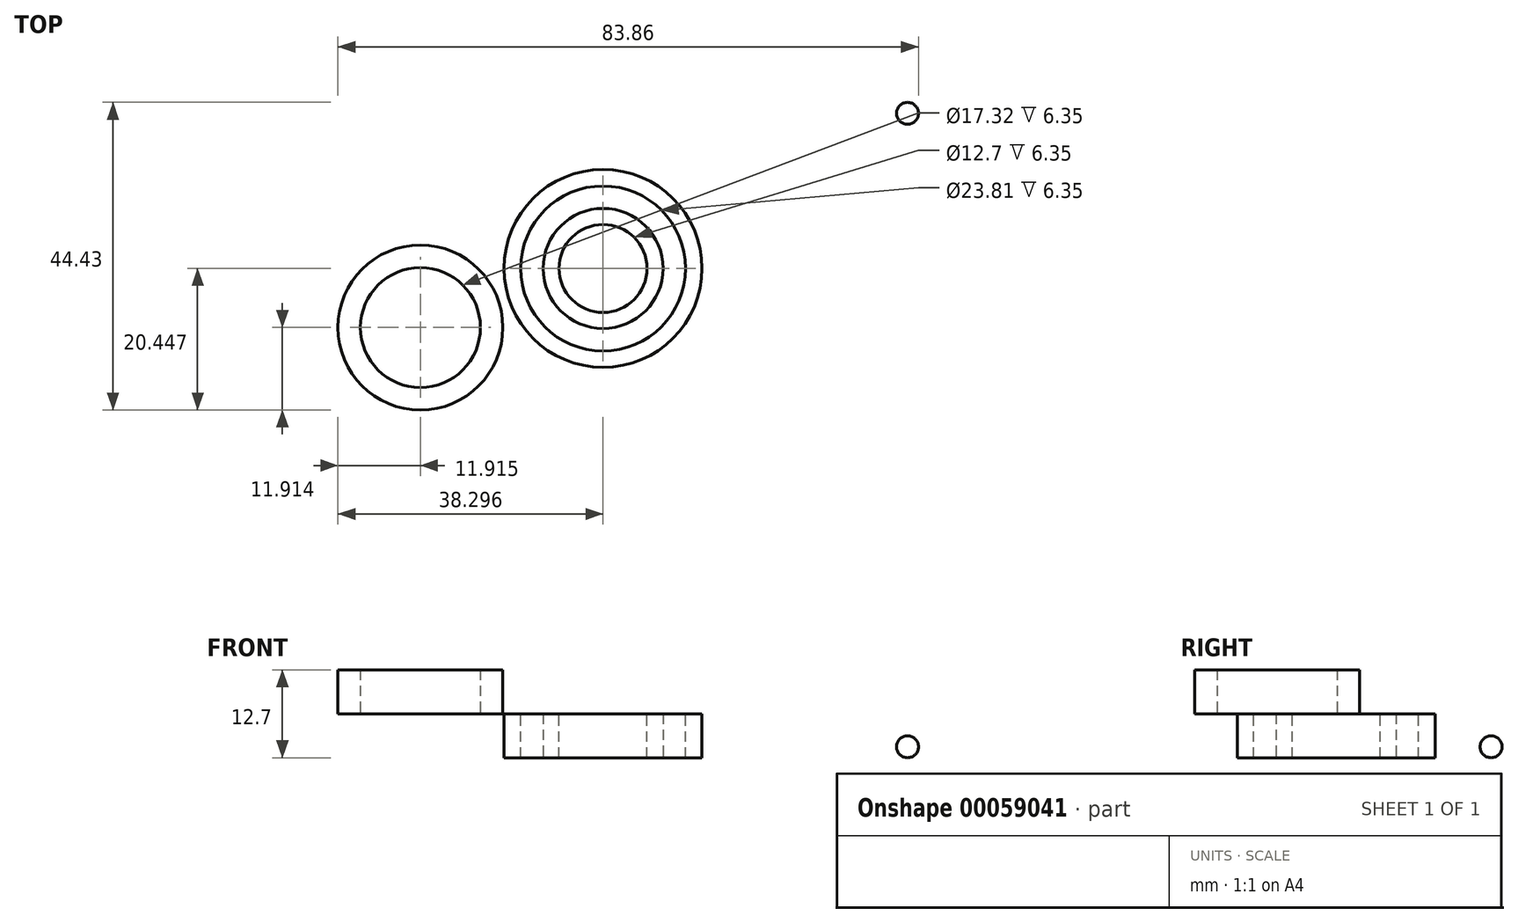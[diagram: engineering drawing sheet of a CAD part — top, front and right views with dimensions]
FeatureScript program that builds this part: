
annotation { "Feature Type Name" : "Feature", "Feature Type Description" : "" }
export const myFeature = defineFeature(function(context is Context, id is Id, definition is map)
    precondition{}
    {
        {
            var Q0;
            Q0=qCreatedBy(makeId("Top.planeOp"),FACE);
            var sketch = newSketch(context, id + "F0", { "sketchPlane" : qUnion([Q0])});
            skCircle(sketch, "E0", {"center": v(-43.97, -22.4) * mm, "radius": 14.29 * mm});
            skSolve(sketch);
        }
        {
            var Q0;
            Q0=makeQuery(id+"F0.imprint","IMPRINT",FACE,{"disambiguationData":[TD([[makeQuery(id+"F0.imprint","IMPRINT",EDGE,{"derivedFrom":sQuery(id+"F0.wireOp",EDGE,"E0")}),1.0]])]});
            extrude(context, id + "F1", {"entities" : qUnion([Q0]), "depth" : 6.35 * mm});
        }
        {
            var Q0;
            Q0=makeQuery(id+"F1.opExtrude","CAP_FACE",FACE,{"disambiguationData":[OSD([sQuery(id+"F0.wireOp",EDGE,"E0")])],"isStart":false});
            var sketch = newSketch(context, id + "F2", { "sketchPlane" : qUnion([Q0])});
            skPoint(sketch, "E1", {"position": v(-43.97, -22.4) * mm});
            skSolve(sketch);
        }
        {
            var Q0;
            Q0=sQuery(id+"F2.wireOp",VERTEX,"E1");
            var Q1;
            Q1=makeQuery(id+"F1.opExtrude","SWEPT_BODY",BODY,{"disambiguationData":[OSD([sQuery(id+"F0.wireOp",EDGE,"E0")])]});
            hole(context, id + "F3", {"style" : HoleStyle.SIMPLE, "holeDiameter" : 23.8 * mm, "endStyle" : HoleEndStyle.THROUGH, "locations" : qUnion([Q0]), "scope" : qUnion([Q1])});
        }
        {
            var Q0;
            Q0=qCreatedBy(makeId("Top.planeOp"),FACE);
            var sketch = newSketch(context, id + "F4", { "sketchPlane" : qUnion([Q0])});
            skCircle(sketch, "E2", {"center": v(-43.97, -22.4) * mm, "radius": 8.66 * mm});
            skSolve(sketch);
        }
        {
            var Q0;
            Q0=makeQuery(id+"F4.imprint","IMPRINT",FACE,{"disambiguationData":[TD([[makeQuery(id+"F4.imprint","IMPRINT",EDGE,{"derivedFrom":sQuery(id+"F4.wireOp",EDGE,"E2")}),1.0]])]});
            extrude(context, id + "F5", {"entities" : qUnion([Q0]), "depth" : 6.35 * mm});
        }
        {
            var Q0;
            Q0=makeQuery(id+"F5.opExtrude","CAP_FACE",FACE,{"disambiguationData":[OSD([sQuery(id+"F4.wireOp",EDGE,"E2")])],"isStart":false});
            var sketch = newSketch(context, id + "F6", { "sketchPlane" : qUnion([Q0])});
            skPoint(sketch, "E3", {"position": v(-43.97, -22.4) * mm});
            skSolve(sketch);
        }
        {
            var Q0;
            Q0=sQuery(id+"F6.wireOp",VERTEX,"E3");
            var Q1;
            Q1=makeQuery(id+"F5.opExtrude","SWEPT_BODY",BODY,{"disambiguationData":[OSD([sQuery(id+"F4.wireOp",EDGE,"E2")])]});
            hole(context, id + "F7", {"style" : HoleStyle.SIMPLE, "holeDiameter" : 12.7 * mm, "endStyle" : HoleEndStyle.THROUGH, "locations" : qUnion([Q0]), "scope" : qUnion([Q1])});
        }
        {
            var Q0;
            Q0=qCreatedBy(makeId("Top.planeOp"),FACE);
            var sketch = newSketch(context, id + "F8", { "sketchPlane" : qUnion([Q0])});
            skCircle(sketch, "E4", {"center": v(0, 0) * mm, "radius": 1.59 * mm});
            skSolve(sketch);
        }
        {
            var Q0;
            Q0=qSketchRegion(id+"F8",true);
            extrude(context, id + "F9", {"entities" : qUnion([Q0]), "depth" : 3.17 * mm});
        }
        {
            var Q0;
            Q0=makeQuery(id+"F9.opExtrude","CAP_EDGE",EDGE,{"disambiguationData":[OSD([sQuery(id+"F8.wireOp",EDGE,"E4")])],"isStart":false});
            var Q1;
            Q1=makeQuery(id+"F9.opExtrude","CAP_EDGE",EDGE,{"disambiguationData":[OSD([sQuery(id+"F8.wireOp",EDGE,"E4")])],"isStart":true});
            fillet(context, id + "F10", {"entities" : qUnion([Q0, Q1]), "radius" : 1.59 * mm, "tangentPropagation" : true, "allowEdgeOverflow" : false});
        }
        {
            var Q0;
            Q0=makeQuery(id+"F1.opExtrude","CAP_FACE",FACE,{"disambiguationData":[OSD([sQuery(id+"F0.wireOp",EDGE,"E0")])],"isStart":false});
            var sketch = newSketch(context, id + "F11", { "sketchPlane" : qUnion([Q0])});
            skCircle(sketch, "E5", {"center": v(-70.36, -30.93) * mm, "radius": 11.91 * mm});
            skSolve(sketch);
        }
        {
            var Q0;
            Q0=makeQuery(id+"F11.imprint","IMPRINT",FACE,{"disambiguationData":[TD([[makeQuery(id+"F11.imprint","IMPRINT",EDGE,{"derivedFrom":sQuery(id+"F11.wireOp",EDGE,"E5")}),1.0]])]});
            extrude(context, id + "F12", {"entities" : qUnion([Q0]), "depth" : 6.35 * mm});
        }
        {
            var Q0;
            Q0=sQuery(id+"F11.wireOp",VERTEX,"E5.center");
            var Q1;
            Q1=makeQuery(id+"F12.opExtrude","SWEPT_BODY",BODY,{"disambiguationData":[OSD([sQuery(id+"F11.wireOp",EDGE,"E5")])]});
            hole(context, id + "F13", {"style" : HoleStyle.SIMPLE, "holeDiameter" : 17.32 * mm, "endStyle" : HoleEndStyle.THROUGH, "oppositeDirection" : true, "locations" : qUnion([Q0]), "scope" : qUnion([Q1])});
        }
    });
